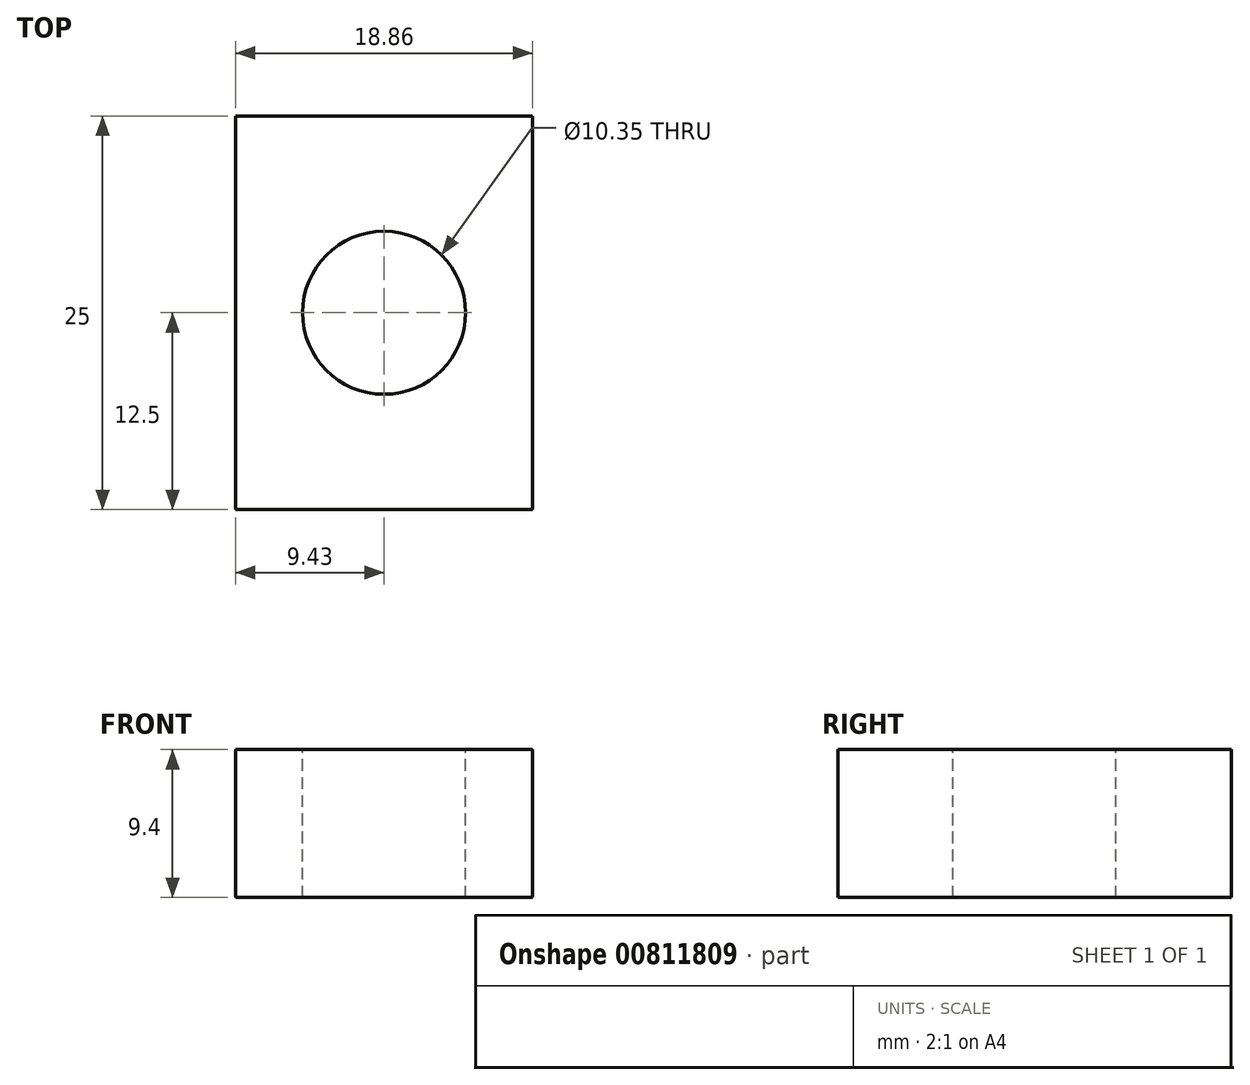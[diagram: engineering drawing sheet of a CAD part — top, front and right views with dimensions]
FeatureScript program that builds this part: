
annotation { "Feature Type Name" : "Feature", "Feature Type Description" : "" }
export const myFeature = defineFeature(function(context is Context, id is Id, definition is map)
    precondition{}
    {
        {
            var Q0;
            Q0=qCreatedBy(makeId("Front.planeOp"),FACE);
            var sketch = newSketch(context, id + "F0", { "sketchPlane" : qUnion([Q0])});
            skLineSegment(sketch, "E0.bottom", {"start": v(9.43, 4.7) * mm, "end": v(-9.43, 4.7) * mm});
            skLineSegment(sketch, "E0.top", {"start": v(9.43, -4.7) * mm, "end": v(-9.43, -4.7) * mm});
            skLineSegment(sketch, "E0.left", {"start": v(9.43, 4.7) * mm, "end": v(9.43, -4.7) * mm});
            skLineSegment(sketch, "E0.right", {"start": v(-9.43, 4.7) * mm, "end": v(-9.43, -4.7) * mm});
            skPoint(sketch, "E0.middle", {"position": v(0, 0) * mm});
            skSolve(sketch);
        }
        {
            var Q0;
            Q0 = qSketchRegion(id + "F0", true);
            extrude(context, id + "F1", {"entities" : qUnion([Q0]), "oppositeDirection" : true, "depth" : 25 * mm, "offsetDistance" : 25 * mm, "symmetric" : true});
        }
        {
            var Q0;
            Q0=makeQuery(id+"F1.opExtrude","SWEPT_FACE",FACE,{"disambiguationData":[OSD([sQuery(id+"F0.wireOp",EDGE,"E0.bottom")])]});
            var sketch = newSketch(context, id + "F2", { "sketchPlane" : qUnion([Q0])});
            skCircle(sketch, "E1", {"center": v(0, 0) * mm, "radius": 5.18 * mm});
            skSolve(sketch);
        }
        {
            var Q0;
            Q0 = qSketchRegion(id + "F2", true);
            extrude(context, id + "F3", {"entities" : qUnion([Q0]), "operationType" : NewBodyOperationType.REMOVE, "oppositeDirection" : true, "depth" : 25 * mm, "offsetDistance" : 25 * mm});
        }
    });
